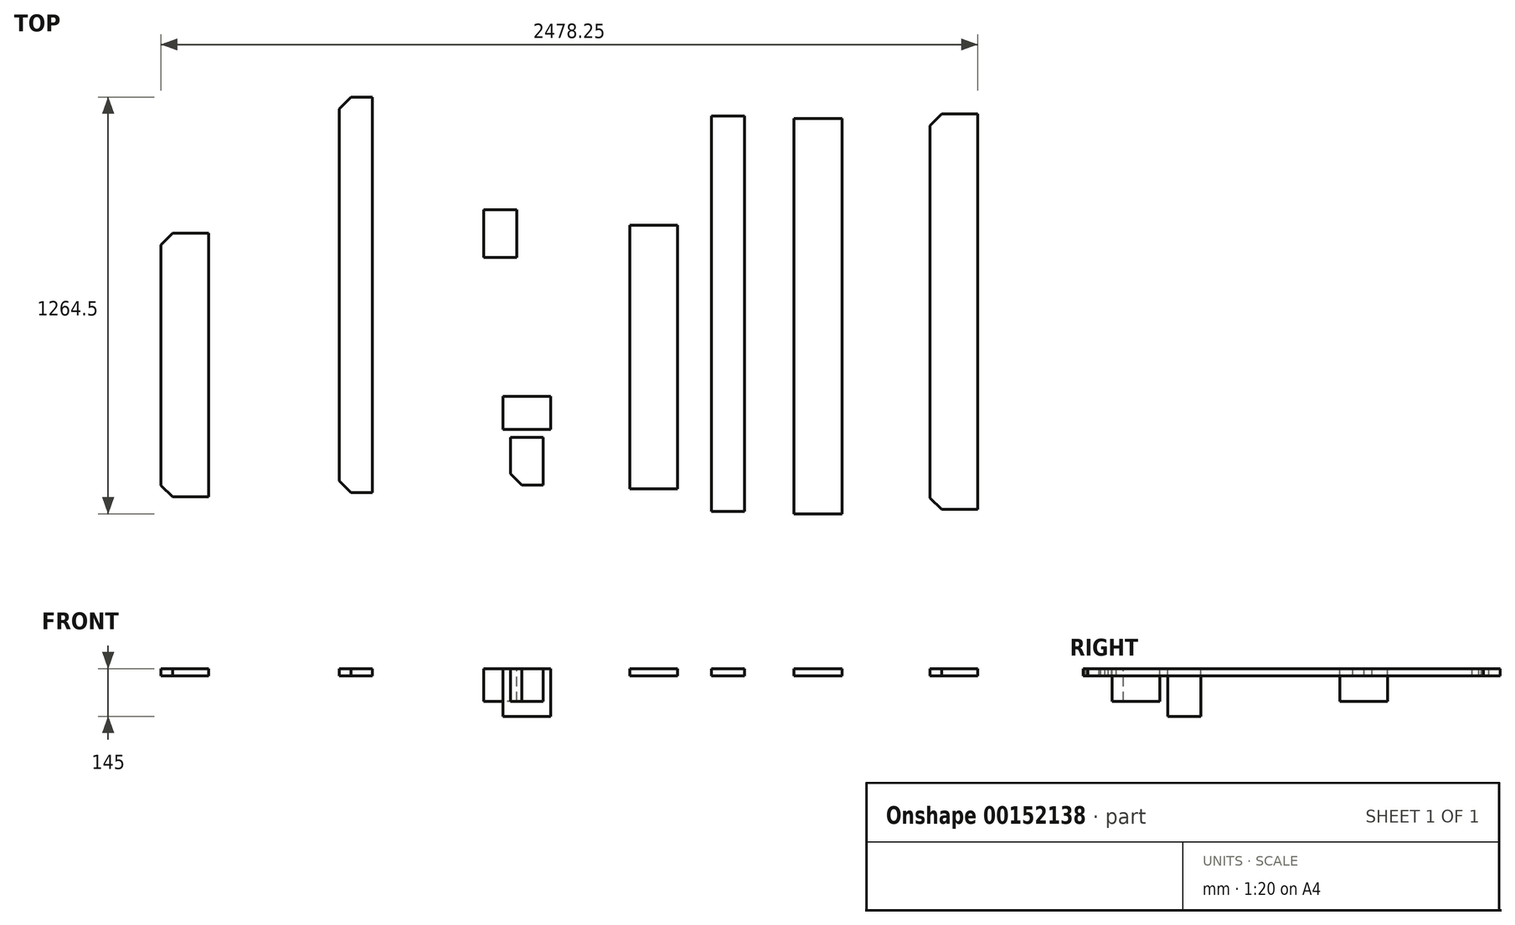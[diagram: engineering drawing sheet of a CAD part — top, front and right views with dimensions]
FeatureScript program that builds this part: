
annotation { "Feature Type Name" : "Feature", "Feature Type Description" : "" }
export const myFeature = defineFeature(function(context is Context, id is Id, definition is map)
    precondition{}
    {
        {
            var Q0;
            Q0=qCreatedBy(makeId("Top.planeOp"),FACE);
            var sketch = newSketch(context, id + "F0", { "sketchPlane" : qUnion([Q0])});
            skLineSegment(sketch, "E0.bottom", {"start": v(72.5, 50) * mm, "end": v(-72.5, 50) * mm});
            skLineSegment(sketch, "E0.top", {"start": v(72.5, -50) * mm, "end": v(-72.5, -50) * mm});
            skLineSegment(sketch, "E0.left", {"start": v(72.5, 50) * mm, "end": v(72.5, -50) * mm});
            skLineSegment(sketch, "E0.right", {"start": v(-72.5, 50) * mm, "end": v(-72.5, -50) * mm});
            skPoint(sketch, "E0.middle", {"position": v(0, 0) * mm});
            skSolve(sketch);
        }
        {
            var Q0;
            Q0=makeQuery(id+"F0.imprint","IMPRINT",FACE,{"disambiguationData":[TD([[makeQuery(id+"F0.imprint","IMPRINT",EDGE,{"derivedFrom":sQuery(id+"F0.wireOp",EDGE,"E0.bottom")}),1.0]])]});
            extrude(context, id + "F1", {"entities" : qUnion([Q0]), "oppositeDirection" : true, "depth" : 145 * mm});
        }
        {
            var Q0;
            Q0=qCreatedBy(makeId("Top.planeOp"),FACE);
            var sketch = newSketch(context, id + "F2", { "sketchPlane" : qUnion([Q0])});
            skLineSegment(sketch, "E1.bottom", {"start": v(50, -74.19) * mm, "end": v(-50, -74.19) * mm});
            skLineSegment(sketch, "E1.top", {"start": v(50, -219.19) * mm, "end": v(-50, -219.19) * mm});
            skLineSegment(sketch, "E1.left", {"start": v(50, -74.19) * mm, "end": v(50, -219.19) * mm});
            skLineSegment(sketch, "E1.right", {"start": v(-50, -74.19) * mm, "end": v(-50, -219.19) * mm});
            skPoint(sketch, "E1.middle", {"position": v(0, -146.69) * mm});
            skSolve(sketch);
        }
        {
            var Q0;
            Q0=makeQuery(id+"F2.imprint","IMPRINT",FACE,{"disambiguationData":[TD([[makeQuery(id+"F2.imprint","IMPRINT",EDGE,{"derivedFrom":sQuery(id+"F2.wireOp",EDGE,"E1.bottom")}),1.0]])]});
            extrude(context, id + "F3", {"entities" : qUnion([Q0]), "oppositeDirection" : true, "depth" : 100 * mm});
        }
        {
            var Q0;
            Q0=makeQuery(id+"F3.opExtrude","SWEPT_EDGE",EDGE,{"disambiguationData":[OSD([sQuery(id+"F2.wireOp",EDGE,"E1.top"),sQuery(id+"F2.wireOp",EDGE,"E1.right")])]});
            chamfer(context, id + "F4", {"entities" : qUnion([Q0]), "width" : 35 * mm, "tangentPropagation" : true});
        }
        {
            var Q0;
            Q0=qCreatedBy(makeId("Top.planeOp"),FACE);
            var sketch = newSketch(context, id + "F5", { "sketchPlane" : qUnion([Q0])});
            skLineSegment(sketch, "E2.bottom", {"start": v(-468.39, -241.54) * mm, "end": v(-568.39, -241.54) * mm});
            skLineSegment(sketch, "E2.top", {"start": v(-468.39, 958.46) * mm, "end": v(-568.39, 958.46) * mm});
            skLineSegment(sketch, "E2.left", {"start": v(-468.39, -241.54) * mm, "end": v(-468.39, 958.46) * mm});
            skLineSegment(sketch, "E2.right", {"start": v(-568.39, -241.54) * mm, "end": v(-568.39, 958.46) * mm});
            skPoint(sketch, "E2.middle", {"position": v(-518.39, 358.46) * mm});
            skSolve(sketch);
        }
        {
            var Q0;
            Q0=makeQuery(id+"F5.imprint","IMPRINT",FACE,{"disambiguationData":[TD([[makeQuery(id+"F5.imprint","IMPRINT",EDGE,{"derivedFrom":sQuery(id+"F5.wireOp",EDGE,"E2.bottom")}),-1.0]])]});
            extrude(context, id + "F6", {"entities" : qUnion([Q0]), "oppositeDirection" : true, "depth" : 22 * mm});
        }
        {
            var Q0;
            Q0=makeQuery(id+"F6.opExtrude","SWEPT_EDGE",EDGE,{"disambiguationData":[OSD([sQuery(id+"F5.wireOp",EDGE,"E2.bottom"),sQuery(id+"F5.wireOp",EDGE,"E2.right")])]});
            chamfer(context, id + "F7", {"entities" : qUnion([Q0]), "width" : 35 * mm, "tangentPropagation" : true});
        }
        {
            var Q0;
            Q0=makeQuery(id+"F6.opExtrude","SWEPT_EDGE",EDGE,{"disambiguationData":[OSD([sQuery(id+"F5.wireOp",EDGE,"E2.top"),sQuery(id+"F5.wireOp",EDGE,"E2.right")])]});
            chamfer(context, id + "F8", {"entities" : qUnion([Q0]), "width" : 35 * mm, "tangentPropagation" : true});
        }
        {
            var Q0;
            Q0=qCreatedBy(makeId("Top.planeOp"),FACE);
            var sketch = newSketch(context, id + "F9", { "sketchPlane" : qUnion([Q0])});
            skLineSegment(sketch, "E3.bottom", {"start": v(456.93, -230.02) * mm, "end": v(311.93, -230.02) * mm});
            skLineSegment(sketch, "E3.top", {"start": v(456.93, 569.98) * mm, "end": v(311.93, 569.98) * mm});
            skLineSegment(sketch, "E3.left", {"start": v(456.93, -230.02) * mm, "end": v(456.93, 569.98) * mm});
            skLineSegment(sketch, "E3.right", {"start": v(311.93, -230.02) * mm, "end": v(311.93, 569.98) * mm});
            skPoint(sketch, "E3.middle", {"position": v(384.43, 169.98) * mm});
            skSolve(sketch);
        }
        {
            var Q0;
            Q0=makeQuery(id+"F9.imprint","IMPRINT",FACE,{"disambiguationData":[TD([[makeQuery(id+"F9.imprint","IMPRINT",EDGE,{"derivedFrom":sQuery(id+"F9.wireOp",EDGE,"E3.bottom")}),-1.0]])]});
            extrude(context, id + "F10", {"entities" : qUnion([Q0]), "oppositeDirection" : true, "depth" : 22 * mm});
        }
        {
            var Q0;
            Q0=qCreatedBy(makeId("Top.planeOp"),FACE);
            var sketch = newSketch(context, id + "F11", { "sketchPlane" : qUnion([Q0])});
            skLineSegment(sketch, "E4.bottom", {"start": v(955.91, -306.04) * mm, "end": v(810.91, -306.04) * mm});
            skLineSegment(sketch, "E4.top", {"start": v(955.91, 893.96) * mm, "end": v(810.91, 893.96) * mm});
            skLineSegment(sketch, "E4.left", {"start": v(955.91, -306.04) * mm, "end": v(955.91, 893.96) * mm});
            skLineSegment(sketch, "E4.right", {"start": v(810.91, -306.04) * mm, "end": v(810.91, 893.96) * mm});
            skPoint(sketch, "E4.middle", {"position": v(883.41, 293.96) * mm});
            skSolve(sketch);
        }
        {
            var Q0;
            Q0=makeQuery(id+"F11.imprint","IMPRINT",FACE,{"disambiguationData":[TD([[makeQuery(id+"F11.imprint","IMPRINT",EDGE,{"derivedFrom":sQuery(id+"F11.wireOp",EDGE,"E4.bottom")}),-1.0]])]});
            extrude(context, id + "F12", {"entities" : qUnion([Q0]), "oppositeDirection" : true, "depth" : 22 * mm});
        }
        {
            var Q0;
            Q0=qCreatedBy(makeId("Top.planeOp"),FACE);
            var sketch = newSketch(context, id + "F13", { "sketchPlane" : qUnion([Q0])});
            skLineSegment(sketch, "E5.bottom", {"start": v(1368.35, -292.79) * mm, "end": v(1223.35, -292.79) * mm});
            skLineSegment(sketch, "E5.top", {"start": v(1368.35, 907.21) * mm, "end": v(1223.35, 907.21) * mm});
            skLineSegment(sketch, "E5.left", {"start": v(1368.35, -292.79) * mm, "end": v(1368.35, 907.21) * mm});
            skLineSegment(sketch, "E5.right", {"start": v(1223.35, -292.79) * mm, "end": v(1223.35, 907.21) * mm});
            skPoint(sketch, "E5.middle", {"position": v(1295.85, 307.21) * mm});
            skSolve(sketch);
        }
        {
            var Q0;
            Q0=makeQuery(id+"F13.imprint","IMPRINT",FACE,{"disambiguationData":[TD([[makeQuery(id+"F13.imprint","IMPRINT",EDGE,{"derivedFrom":sQuery(id+"F13.wireOp",EDGE,"E5.bottom")}),-1.0]])]});
            extrude(context, id + "F14", {"entities" : qUnion([Q0]), "oppositeDirection" : true, "depth" : 22 * mm});
        }
        {
            var Q0;
            Q0=makeQuery(id+"F14.opExtrude","SWEPT_EDGE",EDGE,{"disambiguationData":[OSD([sQuery(id+"F13.wireOp",EDGE,"E5.bottom"),sQuery(id+"F13.wireOp",EDGE,"E5.right")])]});
            var Q1;
            Q1=makeQuery(id+"F14.opExtrude","SWEPT_EDGE",EDGE,{"disambiguationData":[OSD([sQuery(id+"F13.wireOp",EDGE,"E5.top"),sQuery(id+"F13.wireOp",EDGE,"E5.right")])]});
            chamfer(context, id + "F15", {"entities" : qUnion([Q0, Q1]), "width" : 35 * mm, "tangentPropagation" : true});
        }
        {
            var Q0;
            Q0=qCreatedBy(makeId("Top.planeOp"),FACE);
            var sketch = newSketch(context, id + "F16", { "sketchPlane" : qUnion([Q0])});
            skLineSegment(sketch, "E6.bottom", {"start": v(660.42, -299.09) * mm, "end": v(560.42, -299.09) * mm});
            skLineSegment(sketch, "E6.top", {"start": v(660.42, 900.91) * mm, "end": v(560.42, 900.91) * mm});
            skLineSegment(sketch, "E6.left", {"start": v(660.42, -299.09) * mm, "end": v(660.42, 900.91) * mm});
            skLineSegment(sketch, "E6.right", {"start": v(560.42, -299.09) * mm, "end": v(560.42, 900.91) * mm});
            skPoint(sketch, "E6.middle", {"position": v(610.42, 300.91) * mm});
            skSolve(sketch);
        }
        {
            var Q0;
            Q0=makeQuery(id+"F16.imprint","IMPRINT",FACE,{"disambiguationData":[TD([[makeQuery(id+"F16.imprint","IMPRINT",EDGE,{"derivedFrom":sQuery(id+"F16.wireOp",EDGE,"E6.bottom")}),-1.0]])]});
            extrude(context, id + "F17", {"entities" : qUnion([Q0]), "oppositeDirection" : true, "depth" : 22 * mm});
        }
        {
            var Q0;
            Q0=qCreatedBy(makeId("Top.planeOp"),FACE);
            var sketch = newSketch(context, id + "F18", { "sketchPlane" : qUnion([Q0])});
            skLineSegment(sketch, "E7.bottom", {"start": v(-964.9, -254.86) * mm, "end": v(-1109.9, -254.86) * mm});
            skLineSegment(sketch, "E7.top", {"start": v(-964.9, 545.14) * mm, "end": v(-1109.9, 545.14) * mm});
            skLineSegment(sketch, "E7.left", {"start": v(-964.9, -254.86) * mm, "end": v(-964.9, 545.14) * mm});
            skLineSegment(sketch, "E7.right", {"start": v(-1109.9, -254.86) * mm, "end": v(-1109.9, 545.14) * mm});
            skPoint(sketch, "E7.middle", {"position": v(-1037.4, 145.14) * mm});
            skSolve(sketch);
        }
        {
            var Q0;
            Q0=makeQuery(id+"F18.imprint","IMPRINT",FACE,{"disambiguationData":[TD([[makeQuery(id+"F18.imprint","IMPRINT",EDGE,{"derivedFrom":sQuery(id+"F18.wireOp",EDGE,"E7.bottom")}),-1.0]])]});
            extrude(context, id + "F19", {"entities" : qUnion([Q0]), "oppositeDirection" : true, "depth" : 22 * mm});
        }
        {
            var Q0;
            Q0=makeQuery(id+"F19.opExtrude","SWEPT_EDGE",EDGE,{"disambiguationData":[OSD([sQuery(id+"F18.wireOp",EDGE,"E7.bottom"),sQuery(id+"F18.wireOp",EDGE,"E7.right")])]});
            var Q1;
            Q1=makeQuery(id+"F19.opExtrude","SWEPT_EDGE",EDGE,{"disambiguationData":[OSD([sQuery(id+"F18.wireOp",EDGE,"E7.top"),sQuery(id+"F18.wireOp",EDGE,"E7.right")])]});
            chamfer(context, id + "F20", {"entities" : qUnion([Q0, Q1]), "width" : 35 * mm, "tangentPropagation" : true});
        }
        {
            var Q0;
            Q0=qCreatedBy(makeId("Top.planeOp"),FACE);
            var sketch = newSketch(context, id + "F21", { "sketchPlane" : qUnion([Q0])});
            skLineSegment(sketch, "E8.bottom", {"start": v(-30.2, 616.77) * mm, "end": v(-130.2, 616.77) * mm});
            skLineSegment(sketch, "E8.top", {"start": v(-30.2, 471.77) * mm, "end": v(-130.2, 471.77) * mm});
            skLineSegment(sketch, "E8.left", {"start": v(-30.2, 616.77) * mm, "end": v(-30.2, 471.77) * mm});
            skLineSegment(sketch, "E8.right", {"start": v(-130.2, 616.77) * mm, "end": v(-130.2, 471.77) * mm});
            skPoint(sketch, "E8.middle", {"position": v(-80.2, 544.27) * mm});
            skSolve(sketch);
        }
        {
            var Q0;
            Q0=makeQuery(id+"F21.imprint","IMPRINT",FACE,{"disambiguationData":[TD([[makeQuery(id+"F21.imprint","IMPRINT",EDGE,{"derivedFrom":sQuery(id+"F21.wireOp",EDGE,"E8.bottom")}),1.0]])]});
            extrude(context, id + "F22", {"entities" : qUnion([Q0]), "oppositeDirection" : true, "depth" : 100 * mm});
        }
    });
